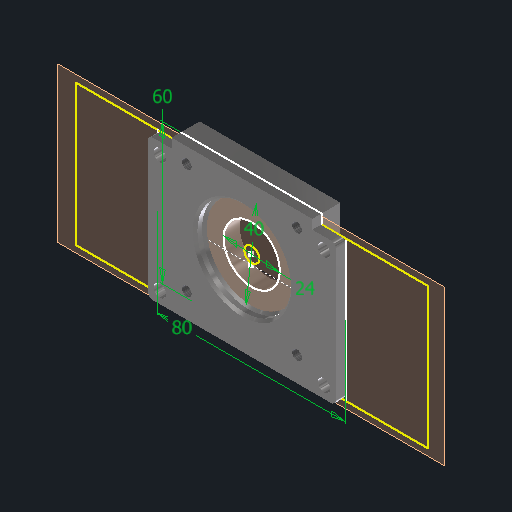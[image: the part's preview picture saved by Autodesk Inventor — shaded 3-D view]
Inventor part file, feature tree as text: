
AUTODESK INVENTOR PART (.ipt)
format: ipt  version: 2022 (Build 260153000, 153)  size: 188,416 bytes
history: native  units: mm
features: reference x10, other x5, sketch x3, chamfer x3, plane x2, extrude x2, hole x2, fillet x1
ambient origin geometry x8: Origin, YZ Plane, XZ Plane, XY Plane, X Axis, Y Axis, Z Axis, Center Point
bodies: Solid1 (feature_tree)
feature tree (28):
  plane  "Work Plane1"
  sketch  "Sketch1"  dims[d0=40.0mm d1=80.0mm]
  extrude  "Extrusion1"  Depth=80.0mm
  plane  "Work Plane2"
  extrude  "Extrusion2"  Depth=60.0mm
  hole  "Hole1"  [1 undecoded]
  hole  "Hole2"  [1 undecoded]
  fillet  "Fillet1"  Radius=4.0mm
  chamfer  "Chamfer1"  Distance=2.0mm
  chamfer  "Chamfer2"  Distance=2.0mm Angle=45.0deg
  chamfer  "Chamfer3"  Distance=24.0mm
  reference  "Reference1"
  reference  "Reference2"
  reference  "Reference3"
  reference  "Reference4"
  reference  "Reference5"
  reference  "Reference6"
  sketch  "Sketch2"  dims[d2=4.0mm d3=0.0mm d4=60.0mm]
  reference  "Reference7"
  reference  "Reference8"
  reference  "Reference9"
  reference  "Reference10"
  sketch  "Sketch3"  dims[d5=8.0mm d6=0.0mm d7=4.134mm d8=8.0mm d9=10.4mm d10=2.0mm d11=90.0deg d12=10.0mm d13=20.594885mm d14=70.0mm d15=50.0mm d16=5.3mm d17=10.0mm d18=10.4mm d19=2.0mm d20=90.0deg d21=12.8mm d22=20.594885mm d23=4.0mm d24=2.0mm d25=1.0mm d26=2.0mm d27=45.0deg d28=24.0mm d29=1.0mm d30=2.0mm d31=45.0deg d32=1.0mm d33=2.0mm d34=45.0deg]
  other  "SistemaDeElevación.iam"
  other  "soporte de rodamientos:1"
  other  "NEMA 23 - 76mm:1"
  other  "Bevel Gears:1"
  other  "Bevel Gear2:1"
note: 2 required parameter values undecoded (feature->parameter linkage not recoverable at this tier; creation-order binding heuristic only, values carry confidence <= 0.55)
